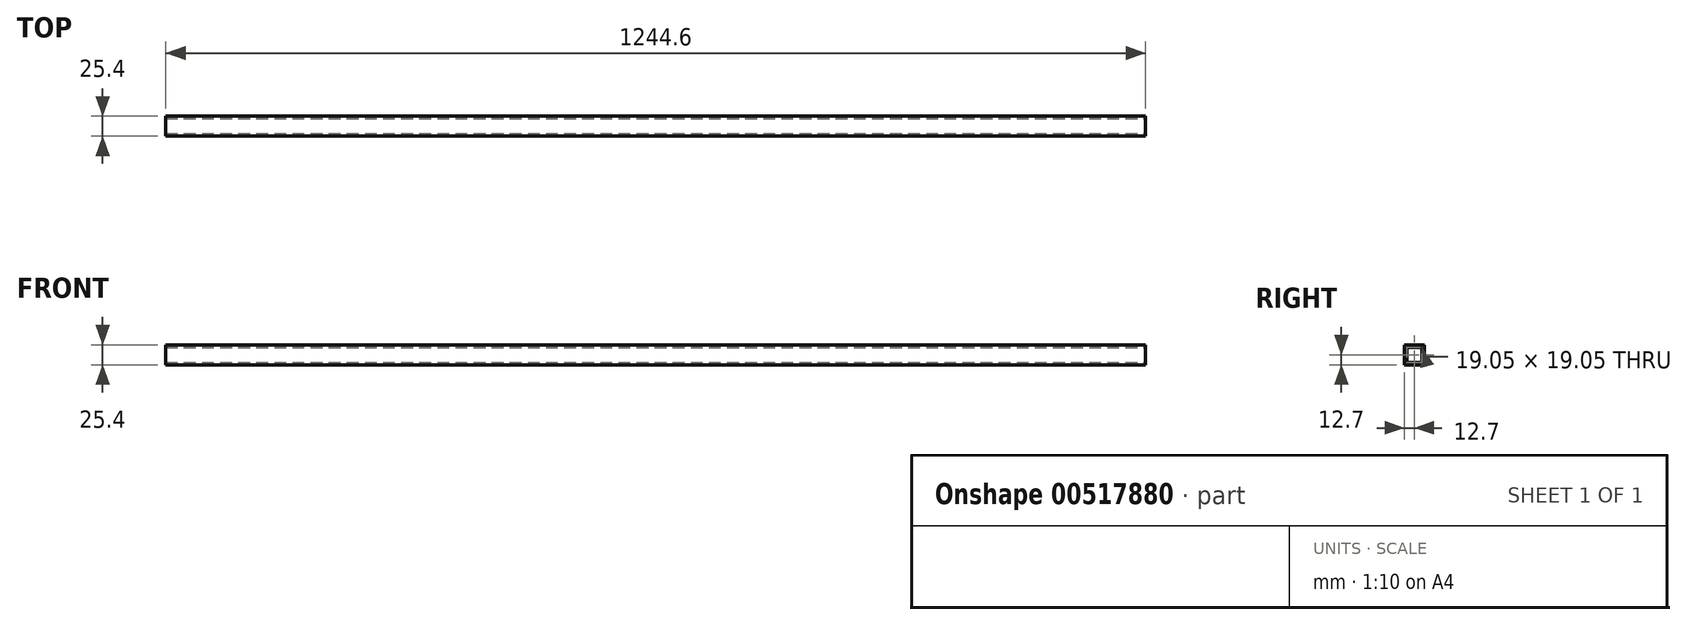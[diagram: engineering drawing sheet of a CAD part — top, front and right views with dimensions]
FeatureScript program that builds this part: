
annotation { "Feature Type Name" : "Feature", "Feature Type Description" : "" }
export const myFeature = defineFeature(function(context is Context, id is Id, definition is map)
    precondition{}
    {
        {
            var Q0;
            Q0=qCreatedBy(makeId("Right.planeOp"),FACE);
            var sketch = newSketch(context, id + "F0", { "sketchPlane" : qUnion([Q0])});
            skLineSegment(sketch, "E0.bottom", {"start": v(0, 0) * mm, "end": v(25.4, 0) * mm});
            skLineSegment(sketch, "E0.top", {"start": v(0, 25.4) * mm, "end": v(25.4, 25.4) * mm});
            skLineSegment(sketch, "E0.left", {"start": v(0, 0) * mm, "end": v(0, 25.4) * mm});
            skLineSegment(sketch, "E0.right", {"start": v(25.4, 0) * mm, "end": v(25.4, 25.4) * mm});
            skLineSegment(sketch, "E1.0", {"start": v(3.17, 22.22) * mm, "end": v(22.22, 22.22) * mm});
            skLineSegment(sketch, "E1.1", {"start": v(3.17, 3.18) * mm, "end": v(3.17, 22.22) * mm});
            skLineSegment(sketch, "E1.2", {"start": v(3.17, 3.18) * mm, "end": v(22.23, 3.18) * mm});
            skLineSegment(sketch, "E1.3", {"start": v(22.23, 3.18) * mm, "end": v(22.22, 22.22) * mm});
            skSolve(sketch);
        }
        {
            var Q0;
            Q0 = qSketchRegion(id + "F0", true);
            extrude(context, id + "F1", {"entities" : qUnion([Q0]), "oppositeDirection" : true, "depth" : 1244.6 * mm, "offsetDistance" : 25.4 * mm});
        }
    });
